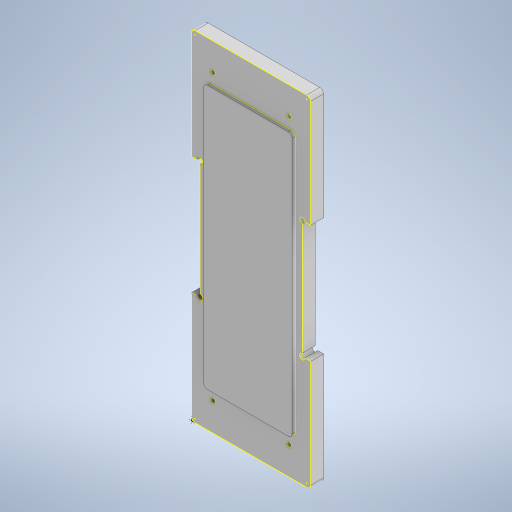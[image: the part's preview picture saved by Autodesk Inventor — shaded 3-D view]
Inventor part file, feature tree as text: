
AUTODESK INVENTOR PART (.ipt)
format: ipt  version: 2024.2 (Build 282272000, 272)  size: 1,389,056 bytes
history: native  units: mm
features: extrude x10, other x5, fillet x3, mirror x2, projected_geometry x2, surface_op x1, sketch x1
ambient origin geometry x8: Origin, YZ Plane, XZ Plane, XY Plane, X Axis, Y Axis, Z Axis, Center Point
bodies: Solid1 (feature_tree)
feature tree (24):
  extrude  "Extrusion1"  Depth=2.0mm
  extrude  "Extrusion2"  Depth=7.04mm TaperAngle=0.0deg
  extrude  "Extrusion3"  Depth=2.0mm
  extrude  "Extrusion4"  Depth=2.0mm
  fillet  "Fillet2"  Radius=1.6mm
  surface_op  "Sculpt1"
  extrude  "Extrusion5"  Depth=2.0mm
  extrude  "Extrusion6"  Depth=2.0mm
  extrude  "Extrusion7"  Depth=2.0mm
  extrude  "Extrusion8"  TaperAngle=0.0deg  [1 undecoded]
  fillet  "Fillet3"  Radius=142.1mm
  mirror  "Mirror1"
  extrude  "Extrusion9"  Depth=2.0mm
  mirror  "Mirror2"
  extrude  "Extrusion10"  Depth=10.0mm TaperAngle=0.0deg
  fillet  "Fillet4"  Radius=2.0mm
  sketch  "Sketch11"  dims[d0=67.0mm d1=186.0mm d2=7.04mm d3=0.0mm d4=48.0mm d5=142.6mm d6=1.6mm d7=0.0mm d9=2.5mm d10=41.0mm d11=153.0mm d12=0.0mm d13=0.0mm d14=142.1mm d16=47.5mm d17=10.0mm d18=0.0mm d19=2.0mm d20=0.0mm d22=0.0mm d23=4.0mm d24=0.0mm d25=0.0mm d26=0.05mm d27=0.5mm d28=0.0mm d30=10.0mm d31=0.0mm d32=4.0mm d33=4.0mm d34=4.0mm d35=10.0mm d36=0.0mm d37=2.0mm d38=2.0mm d39=0.0mm d40=0.0mm d41=1.75mm d42=6.0mm d43=63.5mm d44=3.0mm d45=3.0mm d46=0.0mm d47=0.0mm d49=0.0mm d50=0.0mm d51=2.0mm d52=64.12mm d53=183.0mm]
  projected_geometry  "Projected Loop1"
  projected_geometry  "Projected Loop2"
  other  "Composite1"
  other  "Srf1"
  other  "<userpath>\Google Drive\Unicorn 2020\CAD_V2\Manufacturing\PanelJigAssembly.iam"
  other  "PanelJigAssembly.iam"
  other  "1009799_3D:2"
note: 1 required parameter value undecoded (feature->parameter linkage not recoverable at this tier; creation-order binding heuristic only, values carry confidence <= 0.55)
